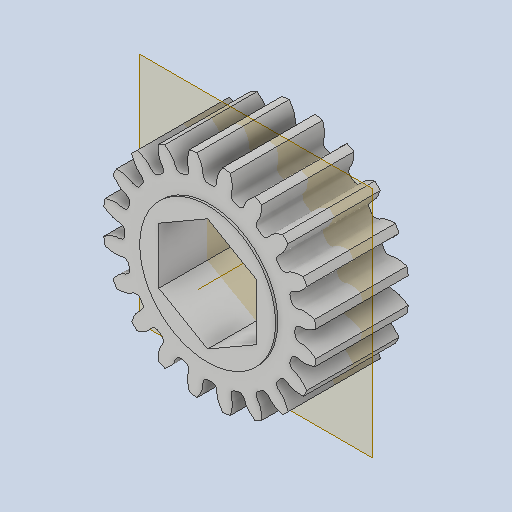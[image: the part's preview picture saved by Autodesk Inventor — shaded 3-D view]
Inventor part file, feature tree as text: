
AUTODESK INVENTOR PART (.ipt)
format: ipt  version: 2023.4 (Build 274418000, 418)  size: 635,904 bytes
history: native  units: in
note: dims shown in document units (in); Inventor stores cm internally (conversion verified against a paired STEP export)
features: plane x1, other x1
ambient origin geometry x8: Origin, YZ Plane, XZ Plane, XY Plane, X Axis, Y Axis, Z Axis, Center Point
bodies: Solid1 (feature_tree)
feature tree (2):
  plane  "Work Plane1"
  other  "Boss-Extrude1"
